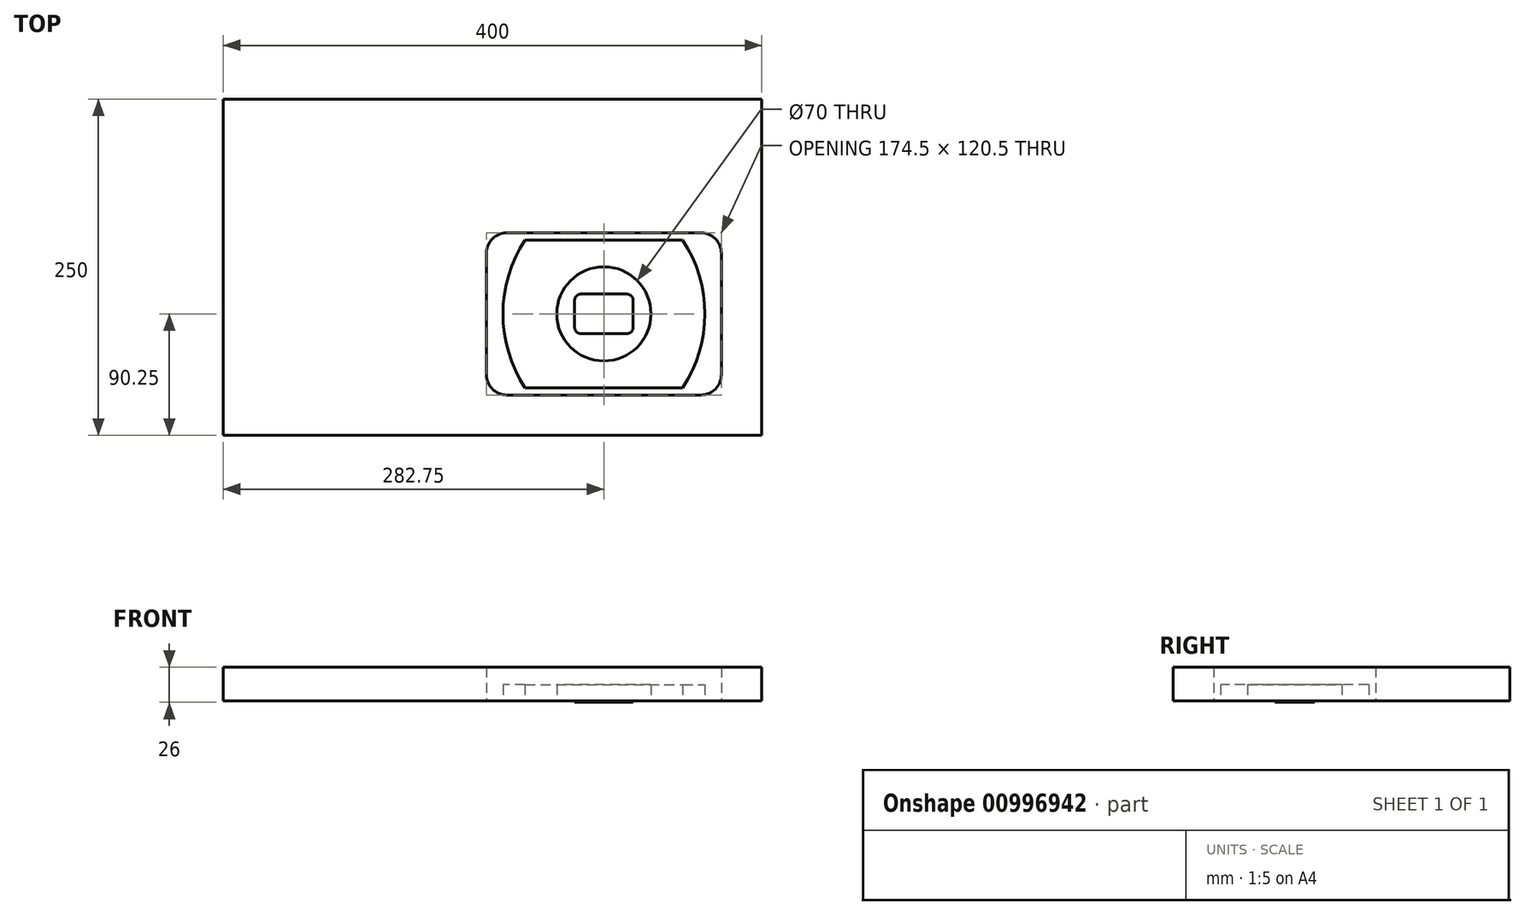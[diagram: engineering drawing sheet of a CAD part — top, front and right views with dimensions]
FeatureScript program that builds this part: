
annotation { "Feature Type Name" : "Feature", "Feature Type Description" : "" }
export const myFeature = defineFeature(function(context is Context, id is Id, definition is map)
    precondition{}
    {
        {
            assignVariable(context, id + "F0", {"name" : "drillDia", "anyValue" : 9.5});
        }
        {
            var Q0;
            Q0=qCreatedBy(makeId("Top.planeOp"),FACE);
            var sketch = newSketch(context, id + "F1", { "sketchPlane" : qUnion([Q0])});
            skLineSegment(sketch, "E0.bottom", {"start": v(-58.52, 55) * mm, "end": v(58.52, 55) * mm});
            skLineSegment(sketch, "E0.top", {"start": v(-58.52, -55) * mm, "end": v(58.52, -55) * mm});
            skPoint(sketch, "E0.middle", {"position": v(0, 0) * mm});
            skArc(sketch, "E1", {"start": v(-58.52, 55) * mm, "mid": v(-75, 0) * mm, "end": v(-58.52, -55) * mm});
            skArc(sketch, "E2.MirrorCS", {"start": v(58.52, 55) * mm, "mid": v(75, 0) * mm, "end": v(58.52, -55) * mm});
            skLineSegment(sketch, "E3.bottom", {"start": v(-87.25, 60.25) * mm, "end": v(87.25, 60.25) * mm});
            skLineSegment(sketch, "E3.top", {"start": v(-87.25, -60.25) * mm, "end": v(87.25, -60.25) * mm});
            skLineSegment(sketch, "E3.left", {"start": v(-87.25, 60.25) * mm, "end": v(-87.25, -60.25) * mm});
            skLineSegment(sketch, "E3.right", {"start": v(87.25, 60.25) * mm, "end": v(87.25, -60.25) * mm});
            skLineSegment(sketch, "E4.bottom", {"start": v(-21.75, 14.75) * mm, "end": v(21.75, 14.75) * mm});
            skLineSegment(sketch, "E4.top", {"start": v(-21.75, -14.75) * mm, "end": v(21.75, -14.75) * mm});
            skLineSegment(sketch, "E4.left", {"start": v(-21.75, 14.75) * mm, "end": v(-21.75, -14.75) * mm});
            skLineSegment(sketch, "E4.right", {"start": v(21.75, 14.75) * mm, "end": v(21.75, -14.75) * mm});
            skLineSegment(sketch, "E5.bottom", {"start": v(-282.75, 159.75) * mm, "end": v(117.25, 159.75) * mm});
            skLineSegment(sketch, "E5.top", {"start": v(-282.75, -90.25) * mm, "end": v(117.25, -90.25) * mm});
            skLineSegment(sketch, "E5.left", {"start": v(-282.75, 159.75) * mm, "end": v(-282.75, -90.25) * mm});
            skLineSegment(sketch, "E5.right", {"start": v(117.25, 159.75) * mm, "end": v(117.25, -90.25) * mm});
            skCircle(sketch, "E6", {"center": v(0, 0) * mm, "radius": 35 * mm});
            skSolve(sketch);
        }
        {
            var Q0;
            Q0=makeQuery(id+"F1.imprint","IMPRINT",FACE,{"disambiguationData":[TD([[makeQuery(id+"F1.imprint","IMPRINT",EDGE,{"derivedFrom":sQuery(id+"F1.wireOp",EDGE,"E3.bottom")}),1.0]])]});
            extrude(context, id + "F2", {"entities" : qUnion([Q0]), "depth" : 25 * mm, "offsetDistance" : 25 * mm});
        }
        {
            var Q0;
            Q0=makeQuery(id+"F1.imprint","IMPRINT",FACE,{"disambiguationData":[TD([[makeQuery(id+"F1.imprint","IMPRINT",EDGE,{"derivedFrom":sQuery(id+"F1.wireOp",EDGE,"E0.bottom")}),-1.0]])]});
            extrude(context, id + "F3", {"entities" : qUnion([Q0]), "depth" : 12 * mm, "offsetDistance" : 25 * mm});
        }
        {
            var Q0;
            Q0=makeQuery(id+"F1.imprint","IMPRINT",FACE,{"disambiguationData":[TD([[makeQuery(id+"F1.imprint","IMPRINT",EDGE,{"derivedFrom":sQuery(id+"F1.wireOp",EDGE,"E4.bottom")}),-1.0]])]});
            var Q1;
            {var subQ0=sQuery(id+"F1.wireOp",EDGE,"E6");var subQ7=sQuery(id+"F1.wireOp",EDGE,"E4.bottom");var subQ8=makeQuery(id+"F1.imprint","INTERSECT",VERTEX,{"disambiguationData":[OD(0.0)],"derivedFrom":[subQ7,subQ0]});Q1=makeQuery(id+"F1.imprint","IMPRINT",FACE,{"disambiguationData":[TD([[makeQuery(id+"F1.imprint","IMPRINT",EDGE,{"disambiguationData":[TD([[subQ8,-1.0]])],"derivedFrom":subQ7}),-1.0]])]});}
            extrude(context, id + "F4", {"entities" : qUnion([Q0, Q1]), "oppositeDirection" : true, "depth" : 1 * mm, "offsetDistance" : 25 * mm});
        }
        {
            var Q0;
            Q0=makeQuery(id+"F4.opExtrude","SWEPT_EDGE",EDGE,{"disambiguationData":[OSD([sQuery(id+"F1.wireOp",EDGE,"E4.top"),sQuery(id+"F1.wireOp",EDGE,"E4.right")])]});
            var Q1;
            Q1=makeQuery(id+"F4.opExtrude","SWEPT_EDGE",EDGE,{"disambiguationData":[OSD([sQuery(id+"F1.wireOp",EDGE,"E4.bottom"),sQuery(id+"F1.wireOp",EDGE,"E4.right")])]});
            var Q2;
            Q2=makeQuery(id+"F4.opExtrude","SWEPT_EDGE",EDGE,{"disambiguationData":[OSD([sQuery(id+"F1.wireOp",EDGE,"E4.top"),sQuery(id+"F1.wireOp",EDGE,"E4.left")])]});
            var Q3;
            Q3=makeQuery(id+"F4.opExtrude","SWEPT_EDGE",EDGE,{"disambiguationData":[OSD([sQuery(id+"F1.wireOp",EDGE,"E4.bottom"),sQuery(id+"F1.wireOp",EDGE,"E4.left")])]});
            fillet(context, id + "F5", {"entities" : qUnion([Q0, Q1, Q2, Q3]), "radius" : (getVariable(context, 'drillDia') / 2) * mm, "tangentPropagation" : true, "allowEdgeOverflow" : false});
        }
        {
            var Q0;
            Q0=makeQuery(id+"F2.opExtrude","SWEPT_EDGE",EDGE,{"disambiguationData":[OSD([sQuery(id+"F1.wireOp",EDGE,"E3.top"),sQuery(id+"F1.wireOp",EDGE,"E3.right")])]});
            var Q1;
            Q1=makeQuery(id+"F2.opExtrude","SWEPT_EDGE",EDGE,{"disambiguationData":[OSD([sQuery(id+"F1.wireOp",EDGE,"E3.bottom"),sQuery(id+"F1.wireOp",EDGE,"E3.right")])]});
            var Q2;
            Q2=makeQuery(id+"F2.opExtrude","SWEPT_EDGE",EDGE,{"disambiguationData":[OSD([sQuery(id+"F1.wireOp",EDGE,"E3.bottom"),sQuery(id+"F1.wireOp",EDGE,"E3.left")])]});
            var Q3;
            Q3=makeQuery(id+"F2.opExtrude","SWEPT_EDGE",EDGE,{"disambiguationData":[OSD([sQuery(id+"F1.wireOp",EDGE,"E3.top"),sQuery(id+"F1.wireOp",EDGE,"E3.left")])]});
            fillet(context, id + "F6", {"entities" : qUnion([Q0, Q1, Q2, Q3]), "radius" : 15 * mm, "tangentPropagation" : true, "allowEdgeOverflow" : false});
        }
    });
